# Revit family: Zumtobel CLEVO
name_source: partatom
category: Lighting Fixtures
revit_build: Autodesk Revit 2018 (Build: 20170223_1515(x64)
units: mm (PartAtom-declared; Revit-internal decimal feet)

## family parameters
Cut with Voids When Loaded = No
Host = Face
Light Source = Yes
OmniClass Number = 23.80.70.11
OmniClass Title = Luminaries for Internal Lighting
Part Type = Normal
Room Calculation Point = No
Round Connector Dimension = Use Diameter
Shared = No

## types (1)
- CLEVO MSC 3400-840 L1580 LDO SR SRG TEC
    Apparent Load = 25 VA
    Assembly Code = D5020200
    Color Filter = 16777215
    Default Elevation = 0 mm  [stored 0 ft]
    Description = LED TEC luminaire
    Dimming Lamp Color Temperature Shift = <None>
    Height = 85 mm
    Lamp = LED
    Length = 1580 mm  [stored 5.18373 ft]
    Manufacturer = Zumtobel Lighting
    Model = 42943073
    Photometric Web File = 42943073_(STD_LEO).IES
    Tilt Angle = 180.00°
    URL = http://www.zumtobel.com
    Voltage = 230 V
    Width = 60 mm

note: [stored X ft] marks values corroborated as IEEE doubles in the binary element streams (Revit-internal decimal feet)

## geometry (parser evidence)
native form markers: Sweep x2
no freeform markers — native parametric forms only
